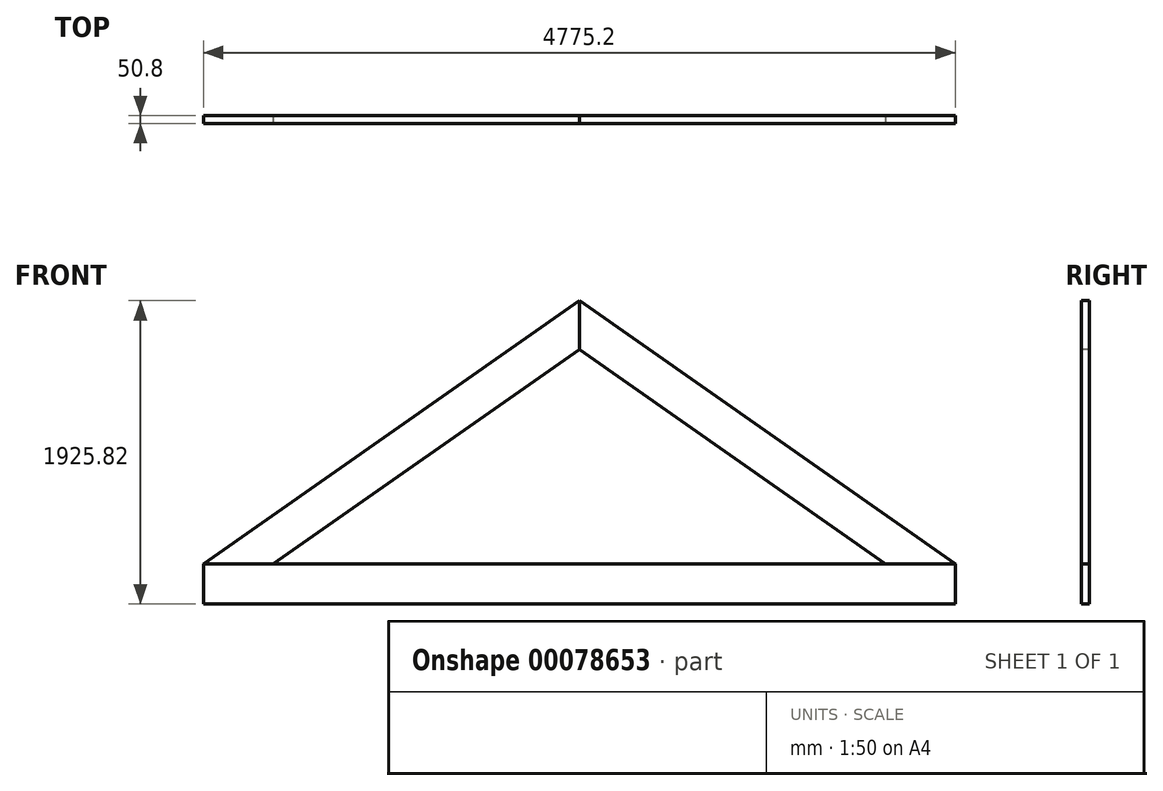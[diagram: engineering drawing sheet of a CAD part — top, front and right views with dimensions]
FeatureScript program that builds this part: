
annotation { "Feature Type Name" : "Feature", "Feature Type Description" : "" }
export const myFeature = defineFeature(function(context is Context, id is Id, definition is map)
    precondition{}
    {
        {
            var Q0;
            Q0=qCreatedBy(makeId("Front.planeOp"),FACE);
            var sketch = newSketch(context, id + "F0", { "sketchPlane" : qUnion([Q0])});
            skLineSegment(sketch, "E0", {"start": v(0, 0) * mm, "end": v(4775.2, 0) * mm});
            skLineSegment(sketch, "E1", {"start": v(4775.2, 0) * mm, "end": v(4775.2, 254) * mm});
            skLineSegment(sketch, "E2", {"start": v(4775.2, 254) * mm, "end": v(0, 254) * mm});
            skLineSegment(sketch, "E3", {"start": v(0, 254) * mm, "end": v(0, 0) * mm});
            skLineSegment(sketch, "E4", {"start": v(0, 254) * mm, "end": v(2387.6, 1925.82) * mm});
            skLineSegment(sketch, "E5", {"start": v(2387.6, 1925.82) * mm, "end": v(4775.2, 254) * mm});
            skLineSegment(sketch, "E6.0", {"start": v(2387.6, 1615.74) * mm, "end": v(4332.36, 254) * mm});
            skLineSegment(sketch, "E6.1", {"start": v(442.84, 254) * mm, "end": v(2387.6, 1615.74) * mm});
            skLineSegment(sketch, "E7", {"start": v(2387.6, 1925.82) * mm, "end": v(2387.6, 1615.74) * mm});
            skSolve(sketch);
        }
        {
            var Q0;
            Q0=makeQuery(id+"F0.imprint","IMPRINT",FACE,{"disambiguationData":[TD([[makeQuery(id+"F0.imprint","IMPRINT",EDGE,{"derivedFrom":sQuery(id+"F0.wireOp",EDGE,"E0")}),1.0]])]});
            extrude(context, id + "F1", {"entities" : qUnion([Q0]), "oppositeDirection" : true, "depth" : 50.8 * mm});
        }
        {
            var Q0;
            {var subQ0=sQuery(id+"F0.wireOp",EDGE,"E4");Q0=makeQuery(id+"F0.imprint","IMPRINT",FACE,{"disambiguationData":[TD([[makeQuery(id+"F0.imprint","IMPRINT",EDGE,{"derivedFrom":subQ0}),-1.0]])]});}
            extrude(context, id + "F2", {"entities" : qUnion([Q0]), "oppositeDirection" : true, "depth" : 50.8 * mm});
        }
        {
            var Q0;
            {var subQ0=sQuery(id+"F0.wireOp",EDGE,"E5");Q0=makeQuery(id+"F0.imprint","IMPRINT",FACE,{"disambiguationData":[TD([[makeQuery(id+"F0.imprint","IMPRINT",EDGE,{"derivedFrom":subQ0}),-1.0]])]});}
            extrude(context, id + "F3", {"entities" : qUnion([Q0]), "oppositeDirection" : true, "depth" : 50.8 * mm});
        }
    });
